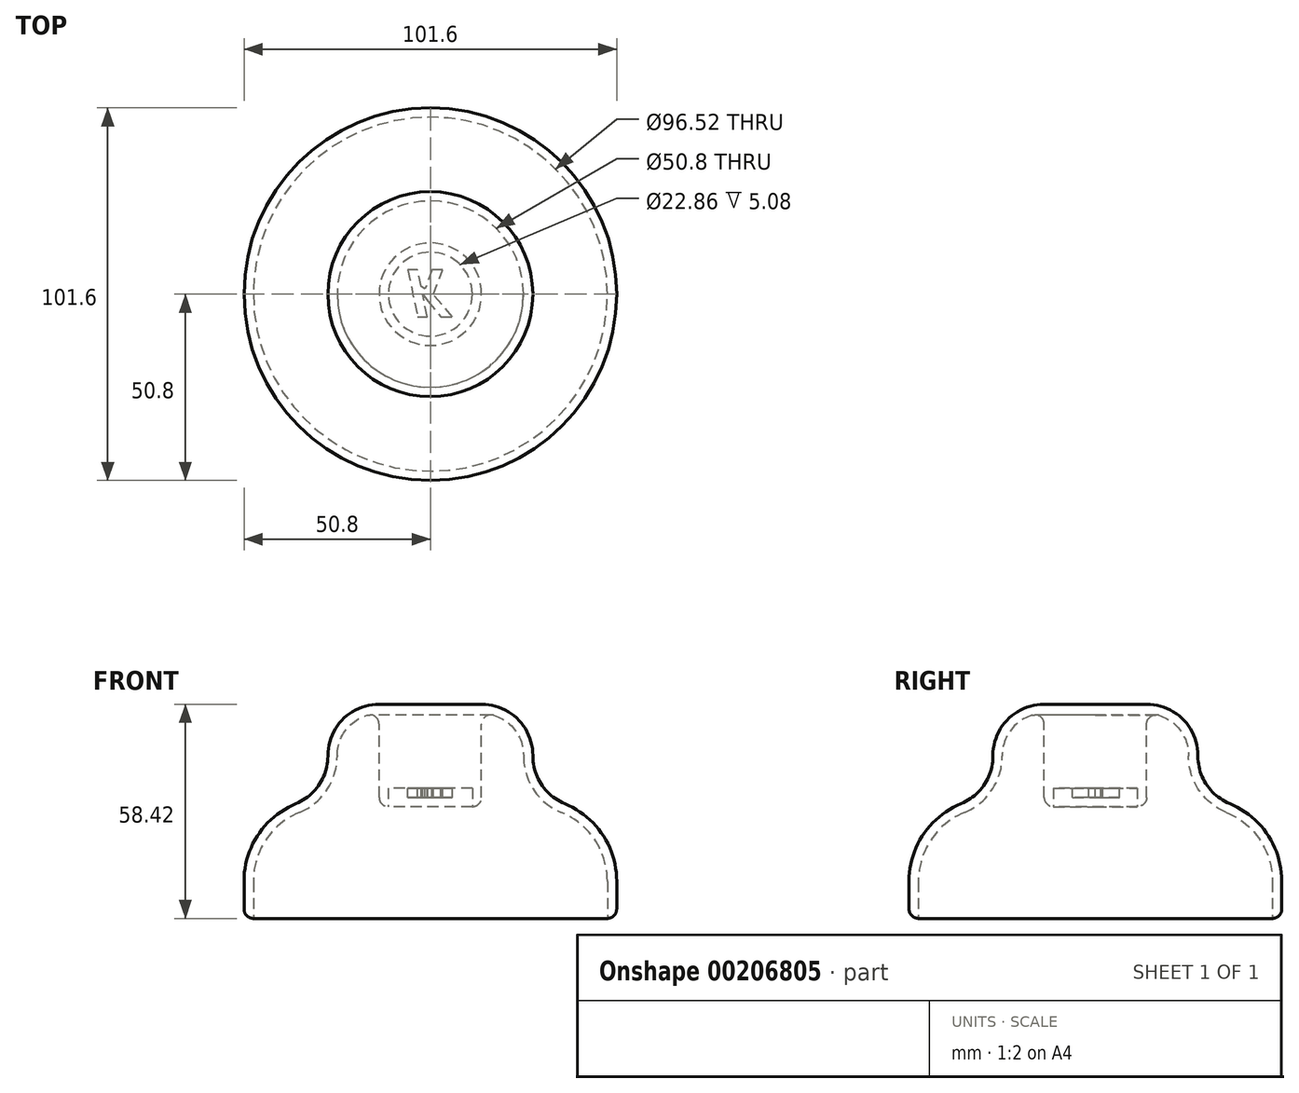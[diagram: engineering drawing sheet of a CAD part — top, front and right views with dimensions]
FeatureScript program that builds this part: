
annotation { "Feature Type Name" : "Feature", "Feature Type Description" : "" }
export const myFeature = defineFeature(function(context is Context, id is Id, definition is map)
    precondition{}
    {
        {
            var Q0;
            Q0=qCreatedBy(makeId("Top.planeOp"),FACE);
            var sketch = newSketch(context, id + "F0", { "sketchPlane" : qUnion([Q0])});
            skCircle(sketch, "E0", {"center": v(0, 0) * mm, "radius": 50.8 * mm});
            skSolve(sketch);
        }
        {
            var Q0;
            Q0=makeQuery(id+"F0.imprint","IMPRINT",FACE,{"disambiguationData":[TD([[makeQuery(id+"F0.imprint","IMPRINT",EDGE,{"derivedFrom":sQuery(id+"F0.wireOp",EDGE,"E0")}),1.0]])]});
            extrude(context, id + "F1", {"entities" : qUnion([Q0]), "depth" : 33.02 * mm});
        }
        {
            var Q0;
            Q0=makeQuery(id+"F1.opExtrude","CAP_FACE",FACE,{"disambiguationData":[OSD([sQuery(id+"F0.wireOp",EDGE,"E0")])],"isStart":false});
            fillet(context, id + "F2", {"entities" : qUnion([Q0]), "radius" : 22.86 * mm, "tangentPropagation" : true, "allowEdgeOverflow" : false});
        }
        {
            var Q0;
            Q0=makeQuery(id+"F1.opExtrude","CAP_EDGE",EDGE,{"disambiguationData":[OSD([sQuery(id+"F0.wireOp",EDGE,"E0")])],"isStart":true});
            fillet(context, id + "F3", {"entities" : qUnion([Q0]), "radius" : 2.54 * mm, "tangentPropagation" : true, "allowEdgeOverflow" : false});
        }
        {
            var Q0;
            Q0=makeQuery(id+"F1.opExtrude","CAP_FACE",FACE,{"disambiguationData":[OSD([sQuery(id+"F0.wireOp",EDGE,"E0")])],"isStart":false});
            extrude(context, id + "F4", {"entities" : qUnion([Q0]), "operationType" : NewBodyOperationType.ADD, "depth" : 25.4 * mm});
        }
        {
            var Q0;
            Q0=makeQuery(id+"F4.opExtrude","SWEPT_FACE",FACE,{"disambiguationData":[OSD([sQuery(id+"F0.wireOp",EDGE,"E0")])]});
            fillet(context, id + "F5", {"entities" : qUnion([Q0]), "radius" : 13.97 * mm, "tangentPropagation" : true, "allowEdgeOverflow" : false});
        }
        {
            var Q0;
            Q0=makeQuery(id+"F1.opExtrude","CAP_FACE",FACE,{"disambiguationData":[OSD([sQuery(id+"F0.wireOp",EDGE,"E0")])],"isStart":true});
            shell(context, id + "F6", {"entities" : qUnion([Q0]), "thickness" : 2.54 * mm});
        }
        {
            var Q0;
            {var subQ0=sQuery(id+"F0.wireOp",EDGE,"E0");Q0=makeQuery(id+"F6.opShell","OFFSET_FACE",FACE,{"disambiguationData":[OSD([subQ0]),TDD([makeQuery(id+"F4.opExtrude","CAP_FACE",FACE,{"disambiguationData":[OSD([subQ0])],"isStart":false})])]});}
            extrude(context, id + "F7", {"entities" : qUnion([Q0]), "operationType" : NewBodyOperationType.ADD, "depth" : 25.4 * mm});
        }
        {
            var Q0;
            Q0=makeQuery(id+"F7.opExtrude","SWEPT_FACE",FACE,{"disambiguationData":[OSD([sQuery(id+"F0.wireOp",EDGE,"E0")])]});
            fillet(context, id + "F8", {"entities" : qUnion([Q0]), "radius" : 2.54 * mm, "tangentPropagation" : true, "allowEdgeOverflow" : false});
        }
        {
            var Q0;
            Q0=makeQuery(id+"F7.opExtrude","CAP_FACE",FACE,{"disambiguationData":[OSD([sQuery(id+"F0.wireOp",EDGE,"E0")])],"isStart":false});
            extrude(context, id + "F9", {"entities" : qUnion([Q0]), "operationType" : NewBodyOperationType.REMOVE, "oppositeDirection" : true, "depth" : 5.08 * mm});
        }
        {
            var Q0;
            Q0=makeQuery(id+"F9.boolean.opBoolean","COPY",FACE,{"derivedFrom":makeQuery(id+"F9.opExtrude","CAP_FACE",FACE,{"disambiguationData":[OSD([sQuery(id+"F0.wireOp",EDGE,"E0")])],"isStart":false})});
            var sketch = newSketch(context, id + "F10", { "sketchPlane" : qUnion([Q0])});
            skText(sketch, "E1", { "text": "K", "fontName": "NotoSans-BoldItalic.ttf"});
            const initialGuessF10  = {"E1": [-0.00662, -0.00662, 1, 0, 0.01293]};
            skSetInitialGuess(sketch, initialGuessF10);
            skSolve(sketch);
        }
        {
            var Q0;
            Q0 = qSketchRegion(id + "F10", true);
            extrude(context, id + "F11", {"entities" : qUnion([Q0]), "operationType" : NewBodyOperationType.ADD, "depth" : 2.54 * mm});
        }
    });
